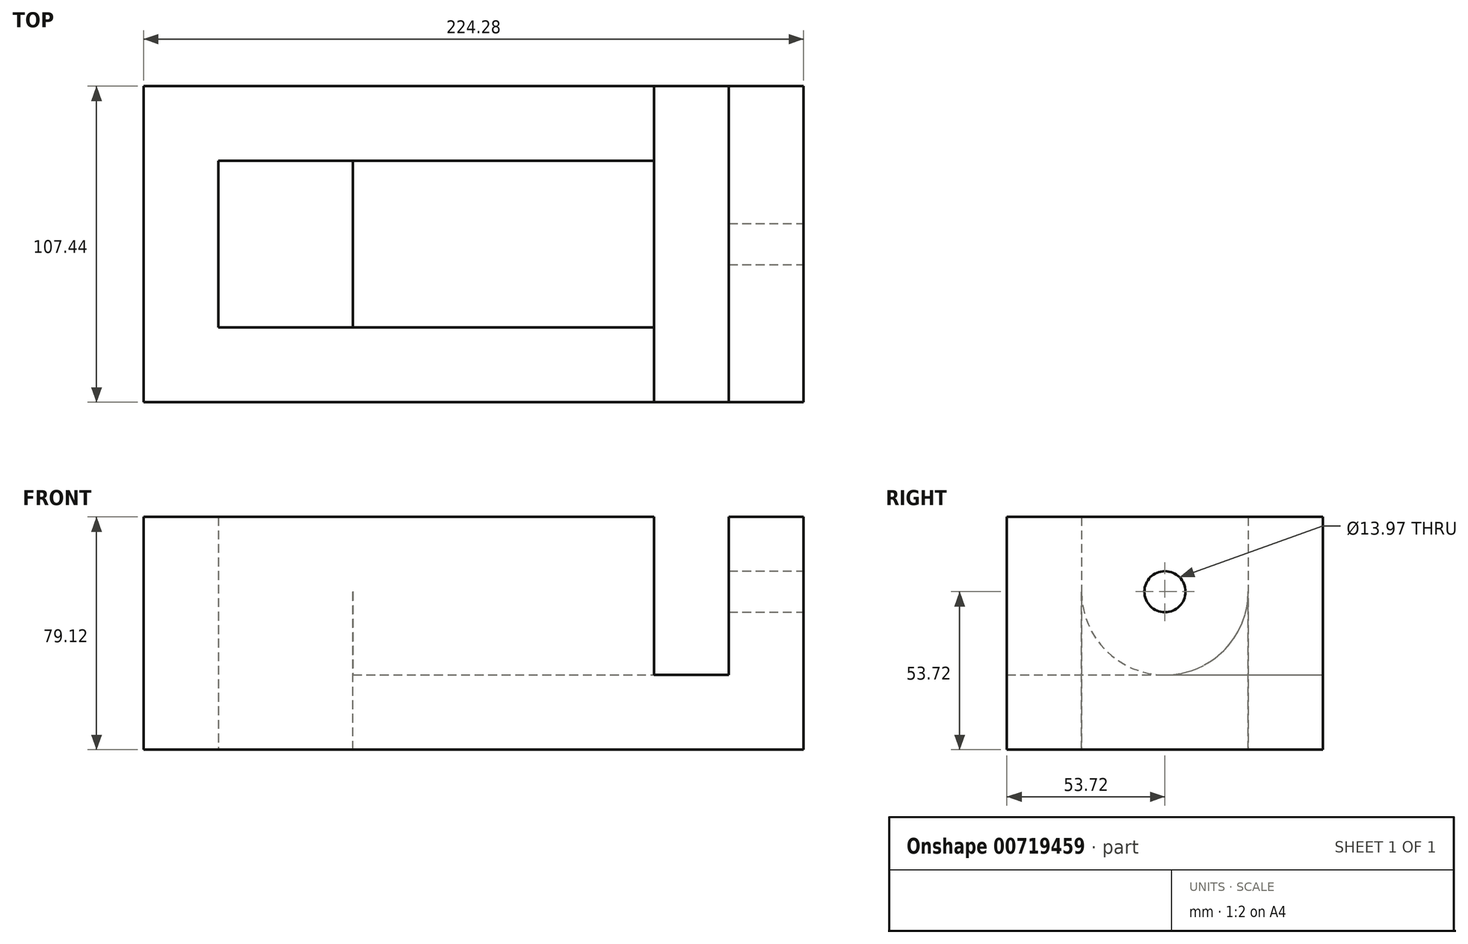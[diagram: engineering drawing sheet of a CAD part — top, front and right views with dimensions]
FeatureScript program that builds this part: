
annotation { "Feature Type Name" : "Feature", "Feature Type Description" : "" }
export const myFeature = defineFeature(function(context is Context, id is Id, definition is map)
    precondition{}
    {
        {
            var Q0;
            Q0=qCreatedBy(makeId("Top.planeOp"),FACE);
            var sketch = newSketch(context, id + "F0", { "sketchPlane" : qUnion([Q0])});
            skLineSegment(sketch, "E0.bottom", {"start": v(61.34, -28.32) * mm, "end": v(-61.34, -28.32) * mm});
            skLineSegment(sketch, "E0.top", {"start": v(61.34, 28.32) * mm, "end": v(-61.34, 28.32) * mm});
            skLineSegment(sketch, "E0.left", {"start": v(61.34, -28.32) * mm, "end": v(61.34, 28.32) * mm});
            skLineSegment(sketch, "E0.right", {"start": v(-61.34, -28.32) * mm, "end": v(-61.34, 28.32) * mm});
            skPoint(sketch, "E0.middle", {"position": v(0, 0) * mm});
            skLineSegment(sketch, "E1.bottom", {"start": v(-86.74, 53.72) * mm, "end": v(137.54, 53.72) * mm});
            skLineSegment(sketch, "E1.top", {"start": v(-86.74, -53.72) * mm, "end": v(137.54, -53.72) * mm});
            skLineSegment(sketch, "E1.left", {"start": v(-86.74, 53.72) * mm, "end": v(-86.74, -53.72) * mm});
            skLineSegment(sketch, "E1.right", {"start": v(137.54, 53.72) * mm, "end": v(137.54, -53.72) * mm});
            skLineSegment(sketch, "E2", {"start": v(61.34, 28.32) * mm, "end": v(112.14, 28.32) * mm});
            skLineSegment(sketch, "E3", {"start": v(61.34, -28.32) * mm, "end": v(112.14, -28.32) * mm});
            skLineSegment(sketch, "E4", {"start": v(112.14, -28.32) * mm, "end": v(112.14, 28.32) * mm});
            skLineSegment(sketch, "E5", {"start": v(-61.34, 0) * mm, "end": v(61.34, 0) * mm});
            skLineSegment(sketch, "E6", {"start": v(61.34, 0) * mm, "end": v(112.14, 0) * mm});
            skLineSegment(sketch, "E7", {"start": v(-15.62, 28.32) * mm, "end": v(-15.62, -28.32) * mm});
            skLineSegment(sketch, "E8", {"start": v(86.74, 28.32) * mm, "end": v(86.74, 53.72) * mm});
            skLineSegment(sketch, "E9", {"start": v(86.74, -28.32) * mm, "end": v(86.74, -53.72) * mm});
            skLineSegment(sketch, "E10", {"start": v(112.14, 28.32) * mm, "end": v(112.14, 53.72) * mm});
            skLineSegment(sketch, "E11", {"start": v(112.14, -28.32) * mm, "end": v(112.14, -53.72) * mm});
            skLineSegment(sketch, "E12", {"start": v(86.74, 28.32) * mm, "end": v(86.74, -28.32) * mm});
            skSolve(sketch);
        }
        {
            var Q0;
            Q0=makeQuery(id+"F0.imprint","IMPRINT",FACE,{"disambiguationData":[TD([[makeQuery(id+"F0.imprint","IMPRINT",EDGE,{"derivedFrom":sQuery(id+"F0.wireOp",EDGE,"E0.bottom")}),1.0]])]});
            var Q1;
            Q1=makeQuery(id+"F0.imprint","IMPRINT",FACE,{"disambiguationData":[TD([[makeQuery(id+"F0.imprint","IMPRINT",EDGE,{"derivedFrom":sQuery(id+"F0.wireOp",EDGE,"E0.bottom")}),-1.0]])]});
            var Q2;
            Q2=makeQuery(id+"F0.imprint","IMPRINT",FACE,{"disambiguationData":[TD([[makeQuery(id+"F0.imprint","IMPRINT",EDGE,{"derivedFrom":sQuery(id+"F0.wireOp",EDGE,"E0.left")}),-1.0]])]});
            var Q3;
            {var subQ0=sQuery(id+"F0.wireOp",EDGE,"E0.top");Q3=makeQuery(id+"F0.imprint","IMPRINT",FACE,{"disambiguationData":[TD([[makeQuery(id+"F0.imprint","IMPRINT",EDGE,{"derivedFrom":subQ0}),1.0]])]});}
            var Q4;
            {var subQ0=sQuery(id+"F0.wireOp",EDGE,"E1.right");Q4=makeQuery(id+"F0.imprint","IMPRINT",FACE,{"disambiguationData":[TD([[makeQuery(id+"F0.imprint","IMPRINT",EDGE,{"derivedFrom":subQ0}),-1.0]])]});}
            var Q5;
            {var subQ0=sQuery(id+"F0.wireOp",EDGE,"E8");Q5=makeQuery(id+"F0.imprint","IMPRINT",FACE,{"disambiguationData":[TD([[makeQuery(id+"F0.imprint","IMPRINT",EDGE,{"derivedFrom":subQ0}),-1.0]])]});}
            var Q6;
            {var subQ0=sQuery(id+"F0.wireOp",EDGE,"E9");Q6=makeQuery(id+"F0.imprint","IMPRINT",FACE,{"disambiguationData":[TD([[makeQuery(id+"F0.imprint","IMPRINT",EDGE,{"derivedFrom":subQ0}),1.0]])]});}
            var Q7;
            {var subQ0=sQuery(id+"F0.wireOp",EDGE,"E4");var subQ5=sQuery(id+"F0.wireOp",EDGE,"E6");var subQ6=makeQuery(id+"F0.imprint","INTERSECT",VERTEX,{"derivedFrom":[subQ0,subQ5]});Q7=makeQuery(id+"F0.imprint","IMPRINT",FACE,{"disambiguationData":[TD([[makeQuery(id+"F0.imprint","IMPRINT",EDGE,{"disambiguationData":[TD([[subQ6,1.0]])],"derivedFrom":subQ5}),-1.0]])]});}
            var Q8;
            {var subQ0=sQuery(id+"F0.wireOp",EDGE,"E4");var subQ5=sQuery(id+"F0.wireOp",EDGE,"E6");var subQ7=makeQuery(id+"F0.imprint","INTERSECT",VERTEX,{"derivedFrom":[subQ0,subQ5]});Q8=makeQuery(id+"F0.imprint","IMPRINT",FACE,{"disambiguationData":[TD([[makeQuery(id+"F0.imprint","IMPRINT",EDGE,{"disambiguationData":[TD([[subQ7,1.0]])],"derivedFrom":subQ5}),1.0]])]});}
            extrude(context, id + "F1", {"entities" : qUnion([Q0, Q1, Q2, Q3, Q4, Q5, Q6, Q7, Q8]), "oppositeDirection" : true, "depth" : 53.72 * mm, "offsetDistance" : 25.4 * mm});
        }
        {
            var Q0;
            {var subQ3=sQuery(id+"F0.wireOp",EDGE,"E6");var subQ5=sQuery(id+"F0.wireOp",EDGE,"E12");var subQ7=makeQuery(id+"F0.imprint","INTERSECT",VERTEX,{"derivedFrom":[subQ3,subQ5]});Q0=makeQuery(id+"F0.imprint","IMPRINT",FACE,{"disambiguationData":[TD([[makeQuery(id+"F0.imprint","IMPRINT",EDGE,{"disambiguationData":[TD([[subQ7,1.0]])],"derivedFrom":subQ3}),1.0]])]});}
            var Q1;
            {var subQ0=sQuery(id+"F0.wireOp",EDGE,"E0.right");var subQ1=sQuery(id+"F0.wireOp",EDGE,"E0.top");var subQ2=makeQuery(id+"F0.imprint","INTERSECT",VERTEX,{"derivedFrom":[subQ1,subQ0]});Q1=makeQuery(id+"F0.imprint","IMPRINT",FACE,{"disambiguationData":[TD([[makeQuery(id+"F0.imprint","IMPRINT",EDGE,{"disambiguationData":[TD([[subQ2,1.0]])],"derivedFrom":subQ1}),1.0]])]});}
            var Q2;
            {var subQ1=sQuery(id+"F0.wireOp",EDGE,"E0.top");var subQ3=sQuery(id+"F0.wireOp",EDGE,"E7");var subQ4=makeQuery(id+"F0.imprint","INTERSECT",VERTEX,{"derivedFrom":[subQ1,subQ3]});Q2=makeQuery(id+"F0.imprint","IMPRINT",FACE,{"disambiguationData":[TD([[makeQuery(id+"F0.imprint","IMPRINT",EDGE,{"disambiguationData":[TD([[subQ4,-1.0]])],"derivedFrom":subQ3}),1.0]])]});}
            var Q3;
            Q3=sQuery(id+"F0.wireOp",EDGE,"E5");
            revolve(context, id + "F2", {"operationType" : NewBodyOperationType.REMOVE, "surfaceOperationType" : NewSurfaceOperationType.NEW, "entities" : qUnion([Q0, Q1, Q2]), "axis" : qUnion([Q3]), "revolveType" : RevolveType.FULL, "oppositeDirection" : true});
        }
        {
            var Q0;
            {var subQ2=sQuery(id+"F0.wireOp",EDGE,"E0.bottom");Q0=makeQuery(id+"F0.imprint","IMPRINT",FACE,{"disambiguationData":[TD([[makeQuery(id+"F0.imprint","IMPRINT",EDGE,{"derivedFrom":subQ2}),1.0]])]});}
            var Q1;
            {var subQ0=sQuery(id+"F0.wireOp",EDGE,"E1.right");Q1=makeQuery(id+"F0.imprint","IMPRINT",FACE,{"disambiguationData":[TD([[makeQuery(id+"F0.imprint","IMPRINT",EDGE,{"derivedFrom":subQ0}),-1.0]])]});}
            extrude(context, id + "F3", {"entities" : qUnion([Q0, Q1]), "operationType" : NewBodyOperationType.ADD, "depth" : 25.4 * mm, "offsetDistance" : 25.4 * mm});
        }
        {
            var Q0;
            {var subQ0=sQuery(id+"F0.wireOp",EDGE,"E0.right");var subQ1=sQuery(id+"F0.wireOp",EDGE,"E0.top");var subQ2=makeQuery(id+"F0.imprint","INTERSECT",VERTEX,{"derivedFrom":[subQ1,subQ0]});Q0=makeQuery(id+"F0.imprint","IMPRINT",FACE,{"disambiguationData":[TD([[makeQuery(id+"F0.imprint","IMPRINT",EDGE,{"disambiguationData":[TD([[subQ2,1.0]])],"derivedFrom":subQ1}),1.0]])]});}
            var Q1;
            {var subQ0=sQuery(id+"F0.wireOp",EDGE,"E0.right");var subQ1=sQuery(id+"F0.wireOp",EDGE,"E0.bottom");var subQ2=makeQuery(id+"F0.imprint","INTERSECT",VERTEX,{"derivedFrom":[subQ1,subQ0]});Q1=makeQuery(id+"F0.imprint","IMPRINT",FACE,{"disambiguationData":[TD([[makeQuery(id+"F0.imprint","IMPRINT",EDGE,{"disambiguationData":[TD([[subQ2,1.0]])],"derivedFrom":subQ1}),-1.0]])]});}
            extrude(context, id + "F4", {"entities" : qUnion([Q0, Q1]), "operationType" : NewBodyOperationType.REMOVE, "oppositeDirection" : true, "depth" : 53.72 * mm, "offsetDistance" : 25.4 * mm});
        }
        {
            var Q0;
            {var subQ0=sQuery(id+"F0.wireOp",EDGE,"E1.right");Q0=makeQuery(id+"F3.boolean.opBoolean","MERGE",FACE,{"derivedFrom":[makeQuery(id+"F1.opExtrude","SWEPT_FACE",FACE,{"disambiguationData":[OSD([subQ0])]}),makeQuery(id+"F3.opExtrude","SWEPT_FACE",FACE,{"disambiguationData":[OSD([subQ0])]})]});}
            var sketch = newSketch(context, id + "F5", { "sketchPlane" : qUnion([Q0])});
            skCircle(sketch, "E13", {"center": v(0, 0) * mm, "radius": 6.99 * mm});
            skSolve(sketch);
        }
        {
            var Q0;
            Q0=makeQuery(id+"F5.imprint","IMPRINT",FACE,{"disambiguationData":[TD([[makeQuery(id+"F5.imprint","IMPRINT",EDGE,{"derivedFrom":sQuery(id+"F5.wireOp",EDGE,"E13")}),1.0]])]});
            extrude(context, id + "F6", {"entities" : qUnion([Q0]), "operationType" : NewBodyOperationType.REMOVE, "oppositeDirection" : true, "depth" : 25.4 * mm, "offsetDistance" : 25.4 * mm});
        }
        {
            var Q0;
            {var subQ0=sQuery(id+"F0.wireOp",EDGE,"E8");Q0=makeQuery(id+"F0.imprint","IMPRINT",FACE,{"disambiguationData":[TD([[makeQuery(id+"F0.imprint","IMPRINT",EDGE,{"derivedFrom":subQ0}),-1.0]])]});}
            var Q1;
            {var subQ0=sQuery(id+"F0.wireOp",EDGE,"E4");var subQ5=sQuery(id+"F0.wireOp",EDGE,"E6");var subQ7=makeQuery(id+"F0.imprint","INTERSECT",VERTEX,{"derivedFrom":[subQ0,subQ5]});Q1=makeQuery(id+"F0.imprint","IMPRINT",FACE,{"disambiguationData":[TD([[makeQuery(id+"F0.imprint","IMPRINT",EDGE,{"disambiguationData":[TD([[subQ7,1.0]])],"derivedFrom":subQ5}),1.0]])]});}
            var Q2;
            {var subQ0=sQuery(id+"F0.wireOp",EDGE,"E4");var subQ5=sQuery(id+"F0.wireOp",EDGE,"E6");var subQ6=makeQuery(id+"F0.imprint","INTERSECT",VERTEX,{"derivedFrom":[subQ0,subQ5]});Q2=makeQuery(id+"F0.imprint","IMPRINT",FACE,{"disambiguationData":[TD([[makeQuery(id+"F0.imprint","IMPRINT",EDGE,{"disambiguationData":[TD([[subQ6,1.0]])],"derivedFrom":subQ5}),-1.0]])]});}
            var Q3;
            {var subQ0=sQuery(id+"F0.wireOp",EDGE,"E9");Q3=makeQuery(id+"F0.imprint","IMPRINT",FACE,{"disambiguationData":[TD([[makeQuery(id+"F0.imprint","IMPRINT",EDGE,{"derivedFrom":subQ0}),1.0]])]});}
            extrude(context, id + "F7", {"entities" : qUnion([Q0, Q1, Q2, Q3]), "operationType" : NewBodyOperationType.REMOVE, "oppositeDirection" : true, "depth" : 28.32 * mm, "offsetDistance" : 25.4 * mm});
        }
    });
